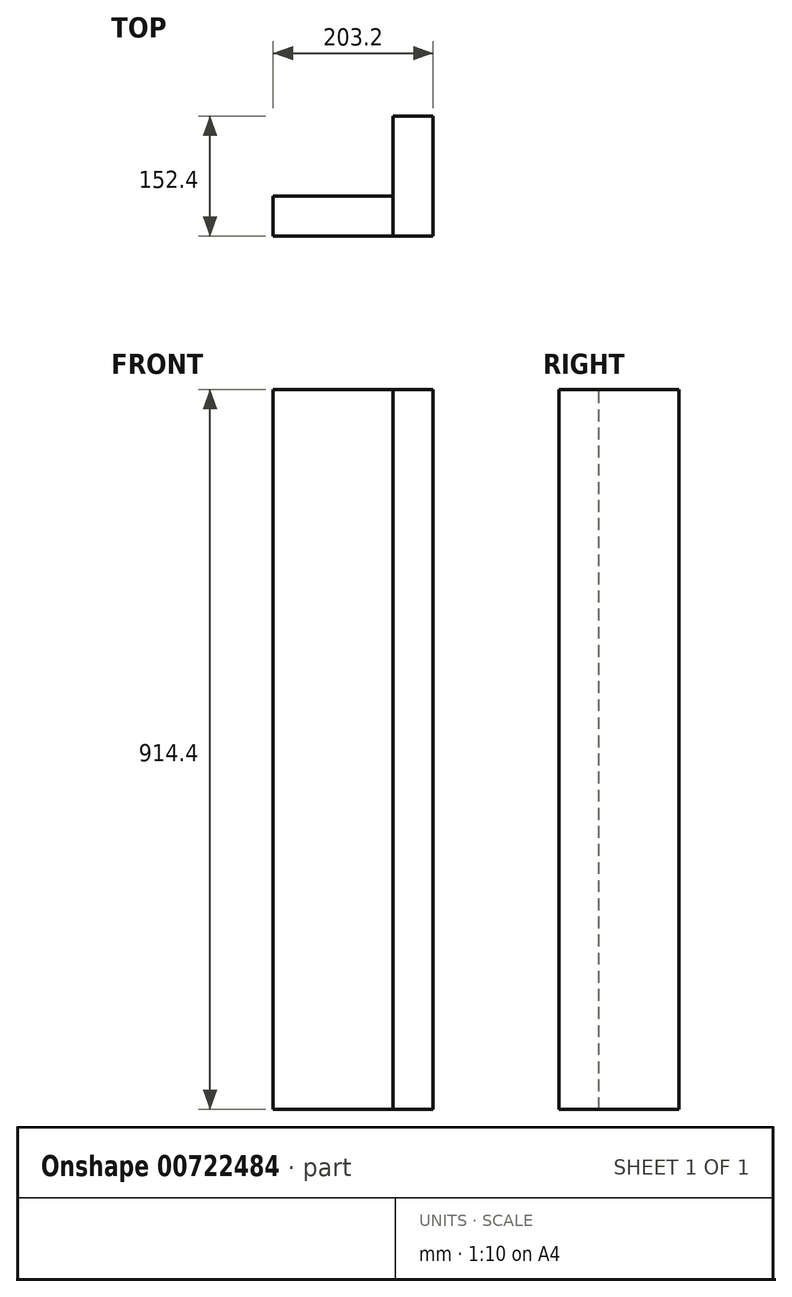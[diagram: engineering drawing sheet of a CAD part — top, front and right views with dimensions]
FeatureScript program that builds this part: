
annotation { "Feature Type Name" : "Feature", "Feature Type Description" : "" }
export const myFeature = defineFeature(function(context is Context, id is Id, definition is map)
    precondition{}
    {
        {
            var Q0;
            Q0=qCreatedBy(makeId("Top.planeOp"),FACE);
            var sketch = newSketch(context, id + "F0", { "sketchPlane" : qUnion([Q0])});
            skLineSegment(sketch, "E0.bottom", {"start": v(0, 0) * mm, "end": v(-152.4, 0) * mm});
            skLineSegment(sketch, "E0.top", {"start": v(0, -50.8) * mm, "end": v(-152.4, -50.8) * mm});
            skLineSegment(sketch, "E0.left", {"start": v(0, 0) * mm, "end": v(0, -50.8) * mm});
            skLineSegment(sketch, "E0.right", {"start": v(-152.4, 0) * mm, "end": v(-152.4, -50.8) * mm});
            skLineSegment(sketch, "E1.bottom", {"start": v(0, -50.8) * mm, "end": v(50.8, -50.8) * mm});
            skLineSegment(sketch, "E1.top", {"start": v(0, 101.6) * mm, "end": v(50.8, 101.6) * mm});
            skLineSegment(sketch, "E1.left", {"start": v(0, -50.8) * mm, "end": v(0, 101.6) * mm});
            skLineSegment(sketch, "E1.right", {"start": v(50.8, -50.8) * mm, "end": v(50.8, 101.6) * mm});
            skSolve(sketch);
        }
        {
            var Q0;
            Q0=makeQuery(id+"F0.imprint","IMPRINT",FACE,{"disambiguationData":[TD([[makeQuery(id+"F0.imprint","IMPRINT",EDGE,{"derivedFrom":sQuery(id+"F0.wireOp",EDGE,"E0.bottom")}),1.0]])]});
            extrude(context, id + "F1", {"entities" : qUnion([Q0]), "oppositeDirection" : true, "depth" : 914.4 * mm, "offsetDistance" : 25.4 * mm});
        }
        {
            var Q0;
            Q0=makeQuery(id+"F0.imprint","IMPRINT",FACE,{"disambiguationData":[TD([[makeQuery(id+"F0.imprint","IMPRINT",EDGE,{"derivedFrom":sQuery(id+"F0.wireOp",EDGE,"E0.left")}),1.0]])]});
            extrude(context, id + "F2", {"entities" : qUnion([Q0]), "oppositeDirection" : true, "depth" : 914.4 * mm, "offsetDistance" : 25.4 * mm});
        }
    });
